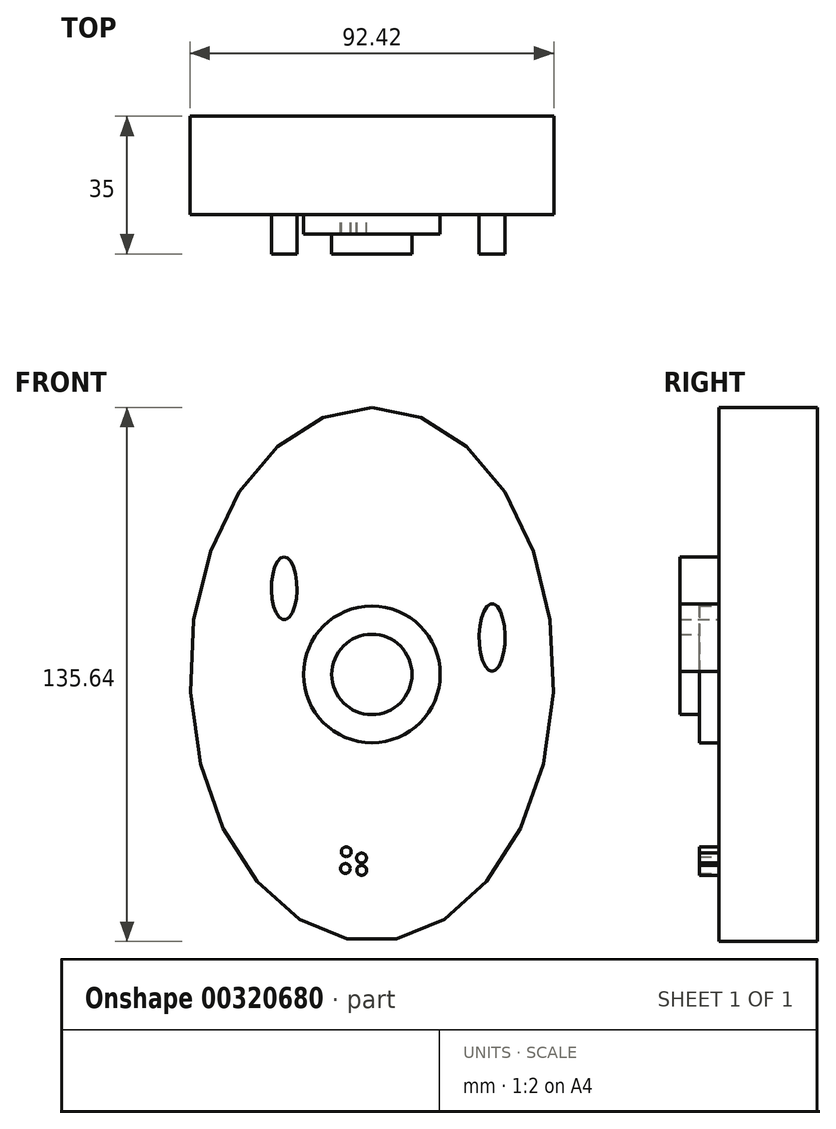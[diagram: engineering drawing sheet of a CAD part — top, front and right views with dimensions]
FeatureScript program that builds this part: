
annotation { "Feature Type Name" : "Feature", "Feature Type Description" : "" }
export const myFeature = defineFeature(function(context is Context, id is Id, definition is map)
    precondition{}
    {
        {
            var Q0;
            Q0=qCreatedBy(makeId("Front.planeOp"),FACE);
            var sketch = newSketch(context, id + "F0", { "sketchPlane" : qUnion([Q0])});
            skEllipse(sketch, "E0", {"center": v(0, 0) * mm, "majorRadius": 67.82 * mm, "minorRadius": 46.2 * mm, "majorAxis": v(0, 1)});
            skSolve(sketch);
        }
        {
            var Q0;
            Q0 = qSketchRegion(id + "F0", true);
            extrude(context, id + "F1", {"entities" : qUnion([Q0]), "depth" : 25 * mm});
        }
        {
            var Q0;
            Q0=makeQuery(id+"F1.opExtrude","CAP_FACE",FACE,{"disambiguationData":[OSD([sQuery(id+"F0.wireOp",EDGE,"E0")])],"isStart":false});
            var sketch = newSketch(context, id + "F2", { "sketchPlane" : qUnion([Q0])});
            skEllipse(sketch, "E1", {"center": v(-22.27, 21.89) * mm, "majorRadius": 7.95 * mm, "minorRadius": 3.26 * mm, "majorAxis": v(0, 1)});
            skSolve(sketch);
        }
        {
            var Q0;
            Q0 = qSketchRegion(id + "F2", true);
            extrude(context, id + "F3", {"entities" : qUnion([Q0]), "operationType" : NewBodyOperationType.ADD, "depth" : 10 * mm});
        }
        {
            var Q0;
            Q0=makeQuery(id+"F1.opExtrude","CAP_FACE",FACE,{"disambiguationData":[OSD([sQuery(id+"F0.wireOp",EDGE,"E0")])],"isStart":false});
            var sketch = newSketch(context, id + "F4", { "sketchPlane" : qUnion([Q0])});
            skCircle(sketch, "E2", {"center": v(0, 0) * mm, "radius": 10.2 * mm});
            skSolve(sketch);
        }
        {
            var Q0;
            Q0 = qSketchRegion(id + "F4", true);
            extrude(context, id + "F5", {"entities" : qUnion([Q0]), "operationType" : NewBodyOperationType.ADD, "depth" : 10 * mm});
        }
        {
            var Q0;
            Q0=makeQuery(id+"F1.opExtrude","CAP_FACE",FACE,{"disambiguationData":[OSD([sQuery(id+"F0.wireOp",EDGE,"E0")])],"isStart":false});
            var sketch = newSketch(context, id + "F6", { "sketchPlane" : qUnion([Q0])});
            skCircle(sketch, "E3", {"center": v(0, 0) * mm, "radius": 17.36 * mm});
            skSolve(sketch);
        }
        {
            var Q0;
            Q0 = qSketchRegion(id + "F6", true);
            extrude(context, id + "F7", {"entities" : qUnion([Q0]), "operationType" : NewBodyOperationType.ADD, "depth" : 5 * mm});
        }
        {
            var Q0;
            Q0=makeQuery(id+"F1.opExtrude","CAP_FACE",FACE,{"disambiguationData":[OSD([sQuery(id+"F0.wireOp",EDGE,"E0")])],"isStart":false});
            var sketch = newSketch(context, id + "F8", { "sketchPlane" : qUnion([Q0])});
            skSolve(sketch);
        }
        {
            var Q0;
            Q0=makeQuery(id+"F8.imprint","IMPRINT",FACE,{"disambiguationData":[TD([[makeQuery(id+"F8.imprint","IMPRINT",EDGE,{"derivedFrom":makeQuery(id+"F1.opExtrude","CAP_EDGE",EDGE,{"disambiguationData":[OSD([sQuery(id+"F0.wireOp",EDGE,"E0")])],"isStart":false})}),1.0]])]});
            var sketch = newSketch(context, id + "F9", { "sketchPlane" : qUnion([Q0])});
            skCircle(sketch, "E4", {"center": v(20.6, -26.74) * mm, "radius": 2.7 * mm});
            skSolve(sketch);
        }
        {
            var Q0;
            Q0=sQuery(id+"F9.wireOp",EDGE,"E4");
            extrude(context, id + "F10", {"bodyType" : ToolBodyType.SURFACE, "surfaceEntities" : qUnion([Q0]), "depth" : 5 * mm});
        }
        {
            var Q0;
            Q0=makeQuery(id+"F8.imprint","IMPRINT",FACE,{"disambiguationData":[TD([[makeQuery(id+"F8.imprint","IMPRINT",EDGE,{"derivedFrom":makeQuery(id+"F1.opExtrude","CAP_EDGE",EDGE,{"disambiguationData":[OSD([sQuery(id+"F0.wireOp",EDGE,"E0")])],"isStart":false})}),1.0]])]});
            var sketch = newSketch(context, id + "F11", { "sketchPlane" : qUnion([Q0])});
            skCircle(sketch, "E5", {"center": v(-18.13, -36.1) * mm, "radius": 3.26 * mm});
            skSolve(sketch);
        }
        {
            var Q0;
            Q0=sQuery(id+"F11.wireOp",EDGE,"E5");
            extrude(context, id + "F12", {"bodyType" : ToolBodyType.SURFACE, "surfaceEntities" : qUnion([Q0]), "depth" : 5 * mm});
        }
        {
            var Q0;
            Q0=makeQuery(id+"F8.imprint","IMPRINT",FACE,{"disambiguationData":[TD([[makeQuery(id+"F8.imprint","IMPRINT",EDGE,{"derivedFrom":makeQuery(id+"F1.opExtrude","CAP_EDGE",EDGE,{"disambiguationData":[OSD([sQuery(id+"F0.wireOp",EDGE,"E0")])],"isStart":false})}),1.0]])]});
            var sketch = newSketch(context, id + "F13", { "sketchPlane" : qUnion([Q0])});
            skCircle(sketch, "E6", {"center": v(22.83, 24.44) * mm, "radius": 3.27 * mm});
            skSolve(sketch);
        }
        {
            var Q0;
            Q0=sQuery(id+"F13.wireOp",EDGE,"E6");
            extrude(context, id + "F14", {"bodyType" : ToolBodyType.SURFACE, "surfaceEntities" : qUnion([Q0]), "depth" : 5 * mm});
        }
        {
            var Q0;
            Q0=makeQuery(id+"F8.imprint","IMPRINT",FACE,{"disambiguationData":[TD([[makeQuery(id+"F8.imprint","IMPRINT",EDGE,{"derivedFrom":makeQuery(id+"F1.opExtrude","CAP_EDGE",EDGE,{"disambiguationData":[OSD([sQuery(id+"F0.wireOp",EDGE,"E0")])],"isStart":false})}),1.0]])]});
            var sketch = newSketch(context, id + "F15", { "sketchPlane" : qUnion([Q0])});
            skCircle(sketch, "E7", {"center": v(-10.12, 46.39) * mm, "radius": 2.24 * mm});
            skSolve(sketch);
        }
        {
            var Q0;
            Q0=sQuery(id+"F15.wireOp",EDGE,"E7");
            extrude(context, id + "F16", {"bodyType" : ToolBodyType.SURFACE, "surfaceEntities" : qUnion([Q0]), "depth" : 5 * mm});
        }
        {
            var Q0;
            Q0=makeQuery(id+"F8.imprint","IMPRINT",FACE,{"disambiguationData":[TD([[makeQuery(id+"F8.imprint","IMPRINT",EDGE,{"derivedFrom":makeQuery(id+"F1.opExtrude","CAP_EDGE",EDGE,{"disambiguationData":[OSD([sQuery(id+"F0.wireOp",EDGE,"E0")])],"isStart":false})}),1.0]])]});
            var sketch = newSketch(context, id + "F17", { "sketchPlane" : qUnion([Q0])});
            skArc(sketch, "E8", {"start": v(-24.86, -8.46) * mm, "mid": v(-29.32, -6.45) * mm, "end": v(-34.14, -7.3) * mm});
            skSolve(sketch);
        }
        {
            var Q0;
            Q0=makeQuery(id+"F8.imprint","IMPRINT",FACE,{"disambiguationData":[TD([[makeQuery(id+"F8.imprint","IMPRINT",EDGE,{"derivedFrom":makeQuery(id+"F1.opExtrude","CAP_EDGE",EDGE,{"disambiguationData":[OSD([sQuery(id+"F0.wireOp",EDGE,"E0")])],"isStart":false})}),1.0]])]});
            var sketch = newSketch(context, id + "F18", { "sketchPlane" : qUnion([Q0])});
            skArc(sketch, "E9", {"start": v(-25.26, -3.8) * mm, "mid": v(-29.36, -5.2) * mm, "end": v(-33.11, -3.03) * mm});
            skSolve(sketch);
        }
        {
            var Q0;
            Q0=makeQuery(id+"F8.imprint","IMPRINT",FACE,{"disambiguationData":[TD([[makeQuery(id+"F8.imprint","IMPRINT",EDGE,{"derivedFrom":makeQuery(id+"F1.opExtrude","CAP_EDGE",EDGE,{"disambiguationData":[OSD([sQuery(id+"F0.wireOp",EDGE,"E0")])],"isStart":false})}),1.0]])]});
            var sketch = newSketch(context, id + "F19", { "sketchPlane" : qUnion([Q0])});
            skArc(sketch, "E10", {"start": v(-34.15, -8.66) * mm, "mid": v(-32.88, -7.37) * mm, "end": v(-31.09, -7.66) * mm});
            skSolve(sketch);
        }
        {
            var Q0;
            Q0=makeQuery(id+"F19.imprint","IMPRINT",FACE,{"disambiguationData":[TD([[makeQuery(id+"F19.imprint","IMPRINT",EDGE,{"derivedFrom":makeQuery(id+"F8.imprint","IMPRINT",EDGE,{"derivedFrom":makeQuery(id+"F1.opExtrude","CAP_EDGE",EDGE,{"disambiguationData":[OSD([sQuery(id+"F0.wireOp",EDGE,"E0")])],"isStart":false})})}),1.0]])]});
            var sketch = newSketch(context, id + "F20", { "sketchPlane" : qUnion([Q0])});
            skArc(sketch, "E11", {"start": v(-27.1, -9.8) * mm, "mid": v(-27.7, -7.74) * mm, "end": v(-29.85, -7.65) * mm});
            skArc(sketch, "E12", {"start": v(-28.84, -9.19) * mm, "mid": v(-30.88, -8.31) * mm, "end": v(-32.92, -9.19) * mm});
            skSolve(sketch);
        }
        {
            var Q0;
            Q0=sQuery(id+"F18.wireOp",EDGE,"E9");
            var Q1;
            Q1=sQuery(id+"F17.wireOp",EDGE,"E8");
            extrude(context, id + "F21", {"bodyType" : ToolBodyType.SURFACE, "surfaceEntities" : qUnion([Q0, Q1]), "depth" : 5 * mm});
        }
        {
            var Q0;
            Q0=sQuery(id+"F19.wireOp",EDGE,"E10");
            var Q1;
            Q1=sQuery(id+"F20.wireOp",EDGE,"E11");
            var Q2;
            Q2=sQuery(id+"F20.wireOp",EDGE,"E12");
            extrude(context, id + "F22", {"bodyType" : ToolBodyType.SURFACE, "surfaceEntities" : qUnion([Q0, Q1, Q2]), "depth" : 5 * mm});
        }
        {
            var Q0;
            Q0=makeQuery(id+"F8.imprint","IMPRINT",FACE,{"disambiguationData":[TD([[makeQuery(id+"F8.imprint","IMPRINT",EDGE,{"derivedFrom":makeQuery(id+"F1.opExtrude","CAP_EDGE",EDGE,{"disambiguationData":[OSD([sQuery(id+"F0.wireOp",EDGE,"E0")])],"isStart":false})}),1.0]])]});
            var sketch = newSketch(context, id + "F23", { "sketchPlane" : qUnion([Q0])});
            skFitSpline(sketch, "E13", {"points": [v(-7.89, -18.15) * mm, v(10.59, -19.72) * mm, v(-8.66, -22.35) * mm, v(0, -23.13) * mm, v(-8.95, -24.55) * mm, v(5.91, -24.4) * mm, v(8.15, -22.3) * mm, v(11.58, -24.12) * mm, v(-8.97, -26.84) * mm, v(11.65, -27.65) * mm, v(5.23, -29.46) * mm, v(12.47, -30.04) * mm, v(4.55, -32.41) * mm, v(0, -29.06) * mm, v(-9.54, -29.13) * mm, v(0, -30.3) * mm, v(-9.74, -31.14) * mm, v(0, -35.66) * mm, v(12.45, -32.91) * mm, v(5.72, -39) * mm, v(-10.14, -35.25) * mm, v(0, -43) * mm, v(12.59, -39.5) * mm], "startDerivative": vector(535.68, -19.52) * mm, "endDerivative": vector(230.11, 151.97) * mm});
            skSolve(sketch);
        }
        {
            var Q0;
            Q0=sQuery(id+"F23.wireOp",EDGE,"E13");
            extrude(context, id + "F24", {"bodyType" : ToolBodyType.SURFACE, "surfaceEntities" : qUnion([Q0]), "depth" : 5 * mm});
        }
        {
            var Q0;
            Q0=makeQuery(id+"F8.imprint","IMPRINT",FACE,{"disambiguationData":[TD([[makeQuery(id+"F8.imprint","IMPRINT",EDGE,{"derivedFrom":makeQuery(id+"F1.opExtrude","CAP_EDGE",EDGE,{"disambiguationData":[OSD([sQuery(id+"F0.wireOp",EDGE,"E0")])],"isStart":false})}),1.0]])]});
            var sketch = newSketch(context, id + "F25", { "sketchPlane" : qUnion([Q0])});
            skCircle(sketch, "E14", {"center": v(-6.5, -45.06) * mm, "radius": 1.25 * mm});
            skCircle(sketch, "E15", {"center": v(-2.62, -46.66) * mm, "radius": 1.25 * mm});
            skCircle(sketch, "E16", {"center": v(-6.73, -49.32) * mm, "radius": 1.25 * mm});
            skCircle(sketch, "E17", {"center": v(-2.57, -49.8) * mm, "radius": 1.25 * mm});
            skSolve(sketch);
        }
        {
            var Q0;
            Q0 = qSketchRegion(id + "F25", true);
            extrude(context, id + "F26", {"entities" : qUnion([Q0]), "operationType" : NewBodyOperationType.ADD, "depth" : 5 * mm});
        }
        {
            var Q0;
            Q0=makeQuery(id+"F8.imprint","IMPRINT",FACE,{"disambiguationData":[TD([[makeQuery(id+"F8.imprint","IMPRINT",EDGE,{"derivedFrom":makeQuery(id+"F1.opExtrude","CAP_EDGE",EDGE,{"disambiguationData":[OSD([sQuery(id+"F0.wireOp",EDGE,"E0")])],"isStart":false})}),1.0]])]});
            var sketch = newSketch(context, id + "F27", { "sketchPlane" : qUnion([Q0])});
            skEllipse(sketch, "E18", {"center": v(30.56, 9.37) * mm, "majorRadius": 8.58 * mm, "minorRadius": 3.3 * mm, "majorAxis": v(0, -1)});
            skSolve(sketch);
        }
        {
            var Q0;
            Q0 = qSketchRegion(id + "F27", true);
            extrude(context, id + "F28", {"entities" : qUnion([Q0]), "operationType" : NewBodyOperationType.ADD, "depth" : 10 * mm});
        }
    });
